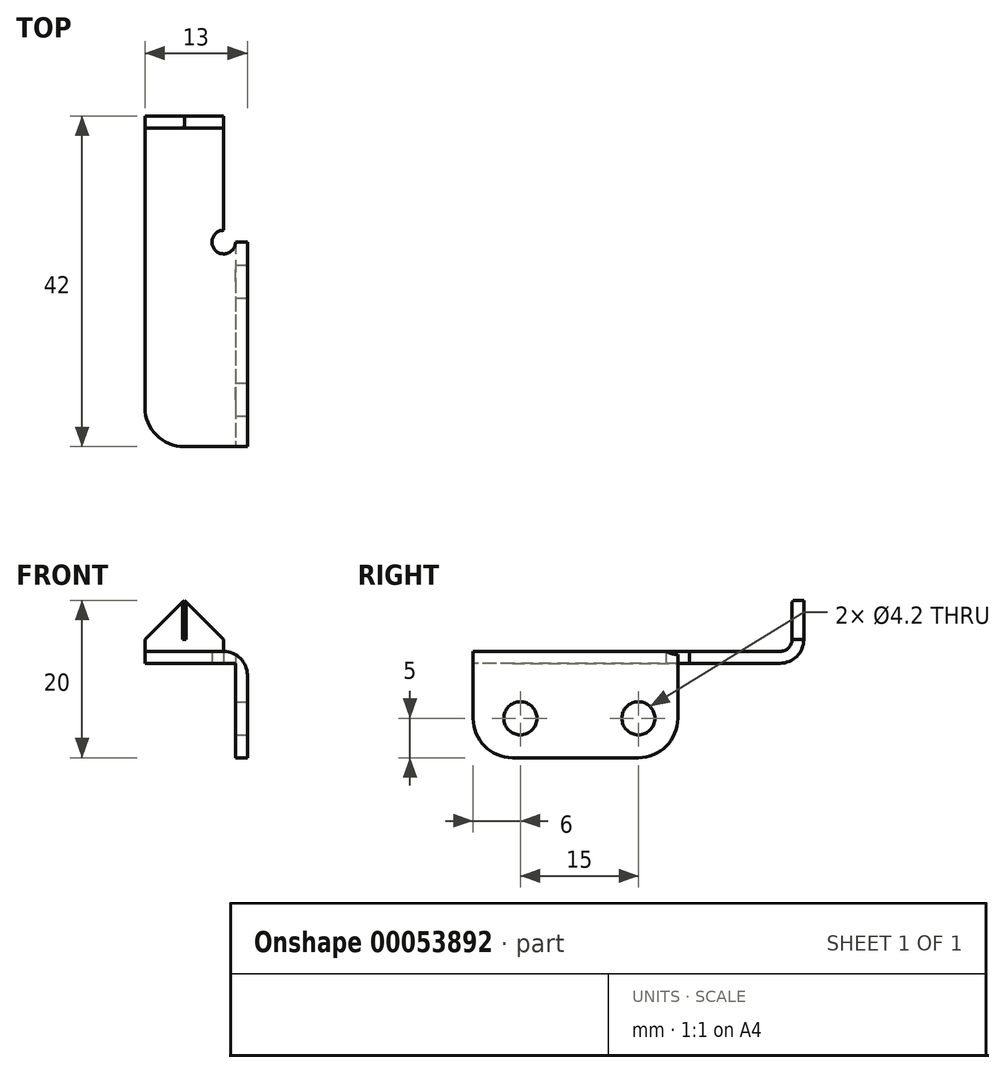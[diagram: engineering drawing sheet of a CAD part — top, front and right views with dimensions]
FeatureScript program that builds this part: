
annotation { "Feature Type Name" : "Feature", "Feature Type Description" : "" }
export const myFeature = defineFeature(function(context is Context, id is Id, definition is map)
    precondition{}
    {
        {
            var Q0;
            Q0=qCreatedBy(makeId("Top.planeOp"),FACE);
            var sketch = newSketch(context, id + "F0", { "sketchPlane" : qUnion([Q0])});
            skLineSegment(sketch, "E0.bottom", {"start": v(0, 0) * mm, "end": v(10, 0) * mm});
            skLineSegment(sketch, "E0.top", {"start": v(0, 42) * mm, "end": v(10, 42) * mm});
            skLineSegment(sketch, "E0.left", {"start": v(0, 0) * mm, "end": v(0, 42) * mm});
            skLineSegment(sketch, "E0.right", {"start": v(10, 0) * mm, "end": v(10, 42) * mm});
            skLineSegment(sketch, "E1", {"start": v(0, 40.5) * mm, "end": v(10, 40.5) * mm});
            skLineSegment(sketch, "E2", {"start": v(10, 26) * mm, "end": v(13, 26) * mm});
            skLineSegment(sketch, "E3", {"start": v(13, 26) * mm, "end": v(13, 0) * mm});
            skLineSegment(sketch, "E4", {"start": v(13, 0) * mm, "end": v(10, 0) * mm});
            skCircle(sketch, "E5", {"center": v(10, 26) * mm, "radius": 1.5 * mm});
            skLineSegment(sketch, "E6", {"start": v(11.5, 26) * mm, "end": v(11.5, 0) * mm});
            skSolve(sketch);
        }
        {
            var Q0;
            {var subQ3=sQuery(id+"F0.wireOp",EDGE,"E0.bottom");Q0=makeQuery(id+"F0.imprint","IMPRINT",FACE,{"disambiguationData":[TD([[makeQuery(id+"F0.imprint","IMPRINT",EDGE,{"derivedFrom":subQ3}),1.0]])]});}
            var Q1;
            {var subQ0=sQuery(id+"F0.wireOp",EDGE,"E0.top");Q1=makeQuery(id+"F0.imprint","IMPRINT",FACE,{"disambiguationData":[TD([[makeQuery(id+"F0.imprint","IMPRINT",EDGE,{"derivedFrom":subQ0}),-1.0]])]});}
            var Q2;
            {var subQ4=sQuery(id+"F0.wireOp",EDGE,"E3");Q2=makeQuery(id+"F0.imprint","IMPRINT",FACE,{"disambiguationData":[TD([[makeQuery(id+"F0.imprint","IMPRINT",EDGE,{"derivedFrom":subQ4}),-1.0]])]});}
            var Q3;
            {var subQ5=sQuery(id+"F0.wireOp",EDGE,"E6");Q3=makeQuery(id+"F0.imprint","IMPRINT",FACE,{"disambiguationData":[TD([[makeQuery(id+"F0.imprint","IMPRINT",EDGE,{"derivedFrom":subQ5}),-1.0]])]});}
            extrude(context, id + "F1", {"entities" : qUnion([Q0, Q1, Q2, Q3]), "depth" : 1.5 * mm});
        }
        {
            var Q0;
            {var subQ0=sQuery(id+"F0.wireOp",EDGE,"E0.top");Q0=makeQuery(id+"F0.imprint","IMPRINT",FACE,{"disambiguationData":[TD([[makeQuery(id+"F0.imprint","IMPRINT",EDGE,{"derivedFrom":subQ0}),-1.0]])]});}
            extrude(context, id + "F2", {"entities" : qUnion([Q0]), "operationType" : NewBodyOperationType.ADD, "depth" : 8 * mm});
        }
        {
            var Q0;
            {var subQ4=sQuery(id+"F0.wireOp",EDGE,"E3");Q0=makeQuery(id+"F0.imprint","IMPRINT",FACE,{"disambiguationData":[TD([[makeQuery(id+"F0.imprint","IMPRINT",EDGE,{"derivedFrom":subQ4}),-1.0]])]});}
            extrude(context, id + "F3", {"entities" : qUnion([Q0]), "operationType" : NewBodyOperationType.ADD, "oppositeDirection" : true, "depth" : 12 * mm});
        }
        {
            var Q0;
            {var subQ0=sQuery(id+"F0.wireOp",EDGE,"E3");Q0=makeQuery(id+"F3.boolean.opBoolean","MERGE",FACE,{"derivedFrom":[makeQuery(id+"F1.opExtrude","SWEPT_FACE",FACE,{"disambiguationData":[OSD([subQ0])]}),makeQuery(id+"F3.opExtrude","SWEPT_FACE",FACE,{"disambiguationData":[OSD([subQ0])]})]});}
            var sketch = newSketch(context, id + "F4", { "sketchPlane" : qUnion([Q0])});
            skCircle(sketch, "E7", {"center": v(6, -7) * mm, "radius": 2.1 * mm});
            skCircle(sketch, "E8", {"center": v(21, -7) * mm, "radius": 2.1 * mm});
            skSolve(sketch);
        }
        {
            var Q0;
            Q0=makeQuery(id+"F4.imprint","IMPRINT",FACE,{"disambiguationData":[TD([[makeQuery(id+"F4.imprint","IMPRINT",EDGE,{"derivedFrom":sQuery(id+"F4.wireOp",EDGE,"E7")}),1.0]])]});
            var Q1;
            Q1=makeQuery(id+"F4.imprint","IMPRINT",FACE,{"disambiguationData":[TD([[makeQuery(id+"F4.imprint","IMPRINT",EDGE,{"derivedFrom":sQuery(id+"F4.wireOp",EDGE,"E8")}),1.0]])]});
            extrude(context, id + "F5", {"entities" : qUnion([Q0, Q1]), "operationType" : NewBodyOperationType.REMOVE, "oppositeDirection" : true, "depth" : 25 * mm});
        }
        {
            var Q0;
            Q0=makeQuery(id+"F2.opExtrude","CAP_EDGE",EDGE,{"disambiguationData":[OSD([sQuery(id+"F0.wireOp",EDGE,"E0.left")])],"isStart":false});
            var Q1;
            Q1=makeQuery(id+"F2.opExtrude","CAP_EDGE",EDGE,{"disambiguationData":[OSD([sQuery(id+"F0.wireOp",EDGE,"E0.right")])],"isStart":false});
            chamfer(context, id + "F6", {"entities" : qUnion([Q0, Q1]), "width" : 5 * mm, "tangentPropagation" : true});
        }
        {
            var Q0;
            Q0=makeQuery(id+"F1.opExtrude","SWEPT_EDGE",EDGE,{"disambiguationData":[OSD([sQuery(id+"F0.wireOp",EDGE,"E0.bottom"),sQuery(id+"F0.wireOp",EDGE,"E0.left")])]});
            var Q1;
            Q1=makeQuery(id+"F3.opExtrude","CAP_EDGE",EDGE,{"disambiguationData":[OSD([sQuery(id+"F0.wireOp",EDGE,"E4")])],"isStart":false});
            var Q2;
            Q2=makeQuery(id+"F3.opExtrude","CAP_EDGE",EDGE,{"disambiguationData":[OSD([sQuery(id+"F0.wireOp",EDGE,"E2")])],"isStart":false});
            fillet(context, id + "F7", {"entities" : qUnion([Q0, Q1, Q2]), "radius" : 5 * mm, "tangentPropagation" : true, "allowEdgeOverflow" : false});
        }
        {
            var Q0;
            Q0=makeQuery(id+"F2.boolean.opBoolean","INTERSECT",EDGE,{"derivedFrom":[makeQuery(id+"F1.opExtrude","CAP_FACE",FACE,{"disambiguationData":[OSD([sQuery(id+"F0.wireOp",EDGE,"E0.bottom"),sQuery(id+"F0.wireOp",EDGE,"E0.top"),sQuery(id+"F0.wireOp",EDGE,"E0.left"),sQuery(id+"F0.wireOp",EDGE,"E0.right"),sQuery(id+"F0.wireOp",EDGE,"E2"),sQuery(id+"F0.wireOp",EDGE,"E3"),sQuery(id+"F0.wireOp",EDGE,"E4")])],"isStart":false}),makeQuery(id+"F2.opExtrude","SWEPT_FACE",FACE,{"disambiguationData":[OSD([sQuery(id+"F0.wireOp",EDGE,"E1")])]})]});
            var Q1;
            Q1=makeQuery(id+"F3.opExtrude","CAP_EDGE",EDGE,{"disambiguationData":[OSD([sQuery(id+"F0.wireOp",EDGE,"E6")])],"isStart":true});
            fillet(context, id + "F8", {"entities" : qUnion([Q0, Q1]), "radius" : 1.5 * mm, "tangentPropagation" : true, "allowEdgeOverflow" : false});
        }
        {
            var Q0;
            Q0=makeQuery(id+"F1.opExtrude","CAP_EDGE",EDGE,{"disambiguationData":[OSD([sQuery(id+"F0.wireOp",EDGE,"E0.top")])],"isStart":true});
            var Q1;
            Q1=makeQuery(id+"F1.opExtrude","CAP_EDGE",EDGE,{"disambiguationData":[OSD([sQuery(id+"F0.wireOp",EDGE,"E3")])],"isStart":false});
            fillet(context, id + "F9", {"entities" : qUnion([Q0, Q1]), "radius" : 3 * mm, "tangentPropagation" : true, "allowEdgeOverflow" : false});
        }
        {
            var Q0;
            Q0=makeQuery(id+"F2.opExtrude","SWEPT_FACE",FACE,{"disambiguationData":[OSD([sQuery(id+"F0.wireOp",EDGE,"E1")])]});
            var sketch = newSketch(context, id + "F10", { "sketchPlane" : qUnion([Q0])});
            skLineSegment(sketch, "E9", {"start": v(5.2, 3) * mm, "end": v(5.2, 7.8) * mm});
            skLineSegment(sketch, "E10", {"start": v(4.8, 3) * mm, "end": v(4.8, 7.8) * mm});
            skSolve(sketch);
        }
        {
            var Q0;
            {var subQ7=sQuery(id+"F10.wireOp",EDGE,"E9");Q0=makeQuery(id+"F10.imprint","IMPRINT",FACE,{"disambiguationData":[TD([[makeQuery(id+"F10.imprint","IMPRINT",EDGE,{"derivedFrom":subQ7}),1.0]])]});}
            extrude(context, id + "F11", {"entities" : qUnion([Q0]), "operationType" : NewBodyOperationType.REMOVE, "oppositeDirection" : true, "depth" : 0.1 * mm});
        }
    });
